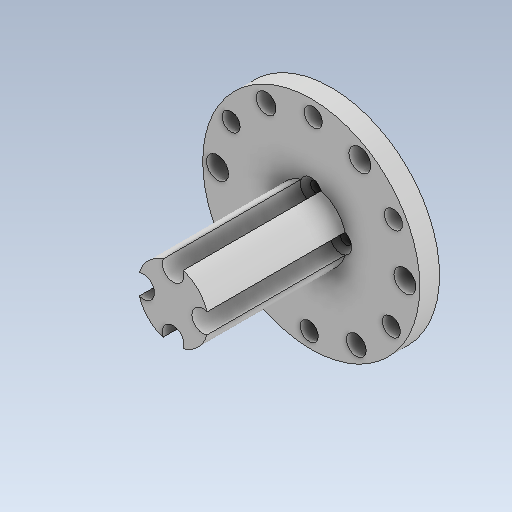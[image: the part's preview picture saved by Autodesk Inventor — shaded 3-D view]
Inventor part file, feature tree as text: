
AUTODESK INVENTOR PART (.ipt)
format: ipt  version: 2020 (Build 240168000, 168)  size: 271,360 bytes
history: native  units: mm
features: reference x12, other x5, extrude x4, sketch x4, fillet x1, hole x1
ambient origin geometry x8: Origin, YZ Plane, XZ Plane, XY Plane, X Axis, Y Axis, Z Axis, Center Point
bodies: Solid1 (feature_tree)
feature tree (27):
  extrude  "Extrusion1"  Depth=35.0mm TaperAngle=0.0deg
  extrude  "Extrusion2"  Depth=5.0mm TaperAngle=0.0deg
  fillet  "Fillet1"  Radius=5.0mm
  extrude  "Extrusion3"  Depth=10.0mm
  hole  "Hole2"  [1 undecoded]
  extrude  "Extrusion4"  [1 undecoded]
  sketch  "Sketch1"  dims[d0=35.0mm d1=2.0mm d2=0.0mm]
  sketch  "Sketch2"  dims[d3=55.0mm d4=5.0mm d5=0.0mm d6=5.0mm]
  sketch  "Sketch3"  dims[d7=10.0mm d8=0.0mm d9=17.9mm]
  reference  "Reference3"
  reference  "Reference4"
  reference  "Reference5"
  reference  "Reference6"
  reference  "Reference7"
  reference  "Reference8"
  reference  "Reference9"
  reference  "Reference10"
  reference  "Reference11"
  reference  "Reference12"
  reference  "Reference13"
  reference  "Reference14"
  sketch  "Sketch5"  dims[d12=15.0mm d20=2.9mm d21=6.0mm d22=5.5mm d23=2.0mm d24=90.0deg d25=20.0mm d26=0.0mm d27=35.0mm d28=0.0mm]
  other  "<userpath>\Desktop\KangKangBalancing\KangKang.iam"
  other  "KangKang.iam"
  other  "100mm-Plastic-Omni-Wheel:1"
  other  "A1_ASM_20"
  other  "F2_19"
note: 2 required parameter values undecoded (feature->parameter linkage not recoverable at this tier; creation-order binding heuristic only, values carry confidence <= 0.55)
